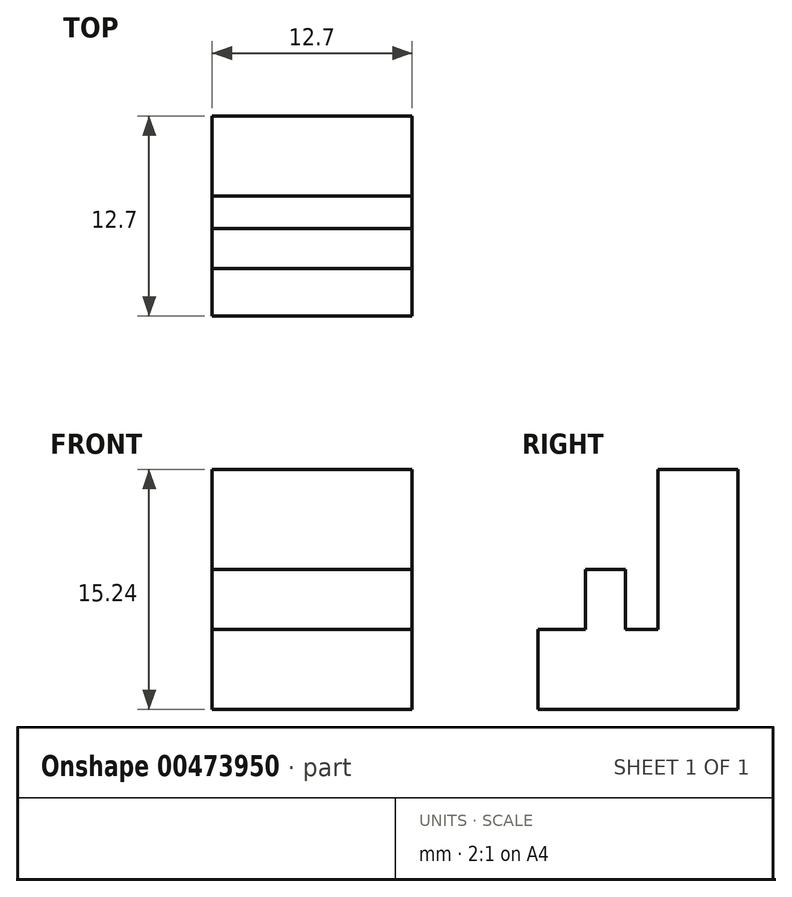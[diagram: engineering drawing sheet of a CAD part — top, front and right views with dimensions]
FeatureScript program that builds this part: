
annotation { "Feature Type Name" : "Feature", "Feature Type Description" : "" }
export const myFeature = defineFeature(function(context is Context, id is Id, definition is map)
    precondition{}
    {
        {
            var Q0;
            Q0=qCreatedBy(makeId("Top.planeOp"),FACE);
            var sketch = newSketch(context, id + "F0", { "sketchPlane" : qUnion([Q0])});
            skLineSegment(sketch, "E0.bottom", {"start": v(-1.38, -5.96) * mm, "end": v(11.32, -5.96) * mm});
            skLineSegment(sketch, "E0.top", {"start": v(-1.38, -18.66) * mm, "end": v(11.32, -18.66) * mm});
            skLineSegment(sketch, "E0.left", {"start": v(-1.38, -5.96) * mm, "end": v(-1.38, -18.66) * mm});
            skLineSegment(sketch, "E0.right", {"start": v(11.32, -5.96) * mm, "end": v(11.32, -18.66) * mm});
            skSolve(sketch);
        }
        {
            var Q0;
            Q0 = qSketchRegion(id + "F0", true);
            extrude(context, id + "F1", {"entities" : qUnion([Q0]), "depth" : 5.08 * mm});
        }
        {
            var Q0;
            Q0=makeQuery(id+"F1.opExtrude","CAP_FACE",FACE,{"disambiguationData":[OSD([sQuery(id+"F0.wireOp",EDGE,"E0.bottom"),sQuery(id+"F0.wireOp",EDGE,"E0.top"),sQuery(id+"F0.wireOp",EDGE,"E0.left"),sQuery(id+"F0.wireOp",EDGE,"E0.right")])],"isStart":false});
            var sketch = newSketch(context, id + "F2", { "sketchPlane" : qUnion([Q0])});
            skLineSegment(sketch, "E1.bottom", {"start": v(-1.38, -5.96) * mm, "end": v(11.32, -5.96) * mm});
            skLineSegment(sketch, "E1.top", {"start": v(-1.38, -11.04) * mm, "end": v(11.32, -11.04) * mm});
            skLineSegment(sketch, "E1.left", {"start": v(-1.38, -5.96) * mm, "end": v(-1.38, -11.04) * mm});
            skLineSegment(sketch, "E1.right", {"start": v(11.32, -5.96) * mm, "end": v(11.32, -11.04) * mm});
            skSolve(sketch);
        }
        {
            var Q0;
            Q0 = qSketchRegion(id + "F2", true);
            extrude(context, id + "F3", {"entities" : qUnion([Q0]), "operationType" : NewBodyOperationType.ADD, "depth" : 10.16 * mm});
        }
        {
            var Q0;
            Q0=makeQuery(id+"F1.opExtrude","CAP_FACE",FACE,{"disambiguationData":[OSD([sQuery(id+"F0.wireOp",EDGE,"E0.bottom"),sQuery(id+"F0.wireOp",EDGE,"E0.top"),sQuery(id+"F0.wireOp",EDGE,"E0.left"),sQuery(id+"F0.wireOp",EDGE,"E0.right")])],"isStart":false});
            var sketch = newSketch(context, id + "F4", { "sketchPlane" : qUnion([Q0])});
            skLineSegment(sketch, "E2.bottom", {"start": v(-1.38, -13.1) * mm, "end": v(11.32, -13.1) * mm});
            skLineSegment(sketch, "E2.top", {"start": v(-1.38, -15.64) * mm, "end": v(11.32, -15.64) * mm});
            skLineSegment(sketch, "E2.left", {"start": v(-1.38, -13.1) * mm, "end": v(-1.38, -15.64) * mm});
            skLineSegment(sketch, "E2.right", {"start": v(11.32, -13.1) * mm, "end": v(11.32, -15.64) * mm});
            skLineSegment(sketch, "E3", {"start": v(-1.38, -11.04) * mm, "end": v(-1.38, -13.1) * mm});
            skSolve(sketch);
        }
        {
            var Q0;
            Q0=makeQuery(id+"F4.imprint","IMPRINT",FACE,{"disambiguationData":[TD([[makeQuery(id+"F4.imprint","IMPRINT",EDGE,{"derivedFrom":sQuery(id+"F4.wireOp",EDGE,"E2.bottom")}),-1.0]])]});
            extrude(context, id + "F5", {"entities" : qUnion([Q0]), "operationType" : NewBodyOperationType.ADD, "depth" : 3.8 * mm});
        }
    });
